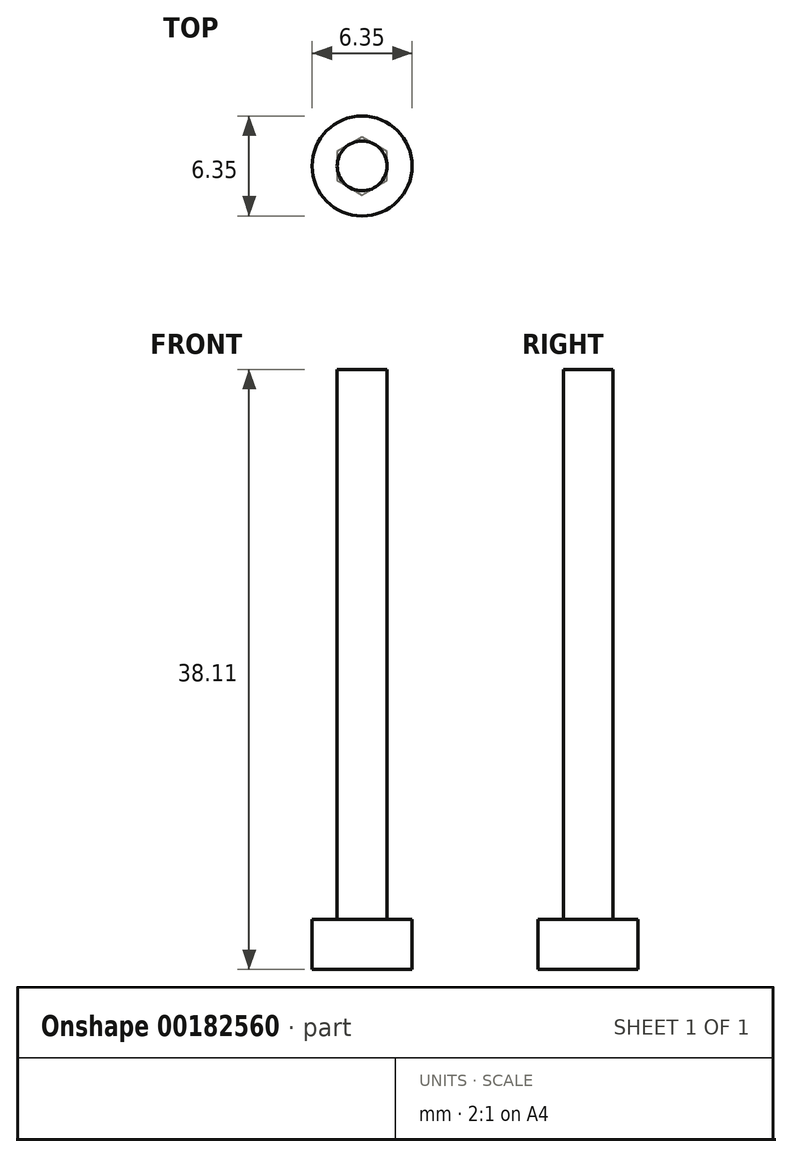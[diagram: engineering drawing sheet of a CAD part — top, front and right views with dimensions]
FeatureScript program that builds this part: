
annotation { "Feature Type Name" : "Feature", "Feature Type Description" : "" }
export const myFeature = defineFeature(function(context is Context, id is Id, definition is map)
    precondition{}
    {
        {
            var Q0;
            Q0=qCreatedBy(makeId("Top.planeOp"),FACE);
            var sketch = newSketch(context, id + "F0", { "sketchPlane" : qUnion([Q0])});
            skCircle(sketch, "E0", {"center": v(-0.07, -10.22) * mm, "radius": 3.18 * mm});
            skSolve(sketch);
        }
        {
            var Q0;
            Q0=makeQuery(id+"F0.imprint","IMPRINT",FACE,{"disambiguationData":[TD([[makeQuery(id+"F0.imprint","IMPRINT",EDGE,{"derivedFrom":sQuery(id+"F0.wireOp",EDGE,"E0")}),1.0]])]});
            var sketch = newSketch(context, id + "F1", { "sketchPlane" : qUnion([Q0])});
            skCircle(sketch, "E1", {"center": v(-0.07, -10.22) * mm, "radius": 1.58 * mm});
            skSolve(sketch);
        }
        {
            var Q0;
            Q0=makeQuery(id+"F1.imprint","IMPRINT",FACE,{"disambiguationData":[TD([[makeQuery(id+"F1.imprint","IMPRINT",EDGE,{"derivedFrom":sQuery(id+"F1.wireOp",EDGE,"E1")}),1.0]])]});
            extrude(context, id + "F2", {"entities" : qUnion([Q0]), "depth" : 34.92 * mm});
        }
        {
            var Q0;
            Q0=makeQuery(id+"F0.imprint","IMPRINT",FACE,{"disambiguationData":[TD([[makeQuery(id+"F0.imprint","IMPRINT",EDGE,{"derivedFrom":sQuery(id+"F0.wireOp",EDGE,"E0")}),1.0]])]});
            extrude(context, id + "F3", {"entities" : qUnion([Q0]), "operationType" : NewBodyOperationType.ADD, "oppositeDirection" : true, "depth" : 3.17 * mm});
        }
        {
            var Q0;
            Q0=makeQuery(id+"F3.opExtrude","CAP_FACE",FACE,{"disambiguationData":[OSD([sQuery(id+"F0.wireOp",EDGE,"E0")])],"isStart":false});
            var sketch = newSketch(context, id + "F4", { "sketchPlane" : qUnion([Q0])});
            skCircle(sketch, "E2.cCircle", {"center": v(-0.07, 10.22) * mm, "radius": 1.59 * mm, "construction": true});
            skLineSegment(sketch, "E2.0", {"start": v(-1.65, 11.14) * mm, "end": v(-0.07, 12.06) * mm});
            skLineSegment(sketch, "E2.1", {"start": v(-0.07, 12.06) * mm, "end": v(1.52, 11.14) * mm});
            skLineSegment(sketch, "E2.2", {"start": v(1.52, 11.14) * mm, "end": v(1.52, 9.3) * mm});
            skLineSegment(sketch, "E2.3", {"start": v(1.52, 9.3) * mm, "end": v(-0.07, 8.4) * mm});
            skLineSegment(sketch, "E2.4", {"start": v(-0.07, 8.4) * mm, "end": v(-1.66, 9.3) * mm});
            skLineSegment(sketch, "E2.5", {"start": v(-1.66, 9.3) * mm, "end": v(-1.65, 11.14) * mm});
            skPoint(sketch, "E2.0.midPoint", {"position": v(-0.86, 11.6) * mm});
            skSolve(sketch);
        }
        {
            var Q0;
            Q0=makeQuery(id+"F4.imprint","IMPRINT",FACE,{"disambiguationData":[TD([[makeQuery(id+"F4.imprint","IMPRINT",EDGE,{"derivedFrom":sQuery(id+"F4.wireOp",EDGE,"E2.0")}),-1.0]])]});
            extrude(context, id + "F5", {"entities" : qUnion([Q0]), "operationType" : NewBodyOperationType.REMOVE, "oppositeDirection" : true, "depth" : 3 / 965.2 * mm});
        }
    });
